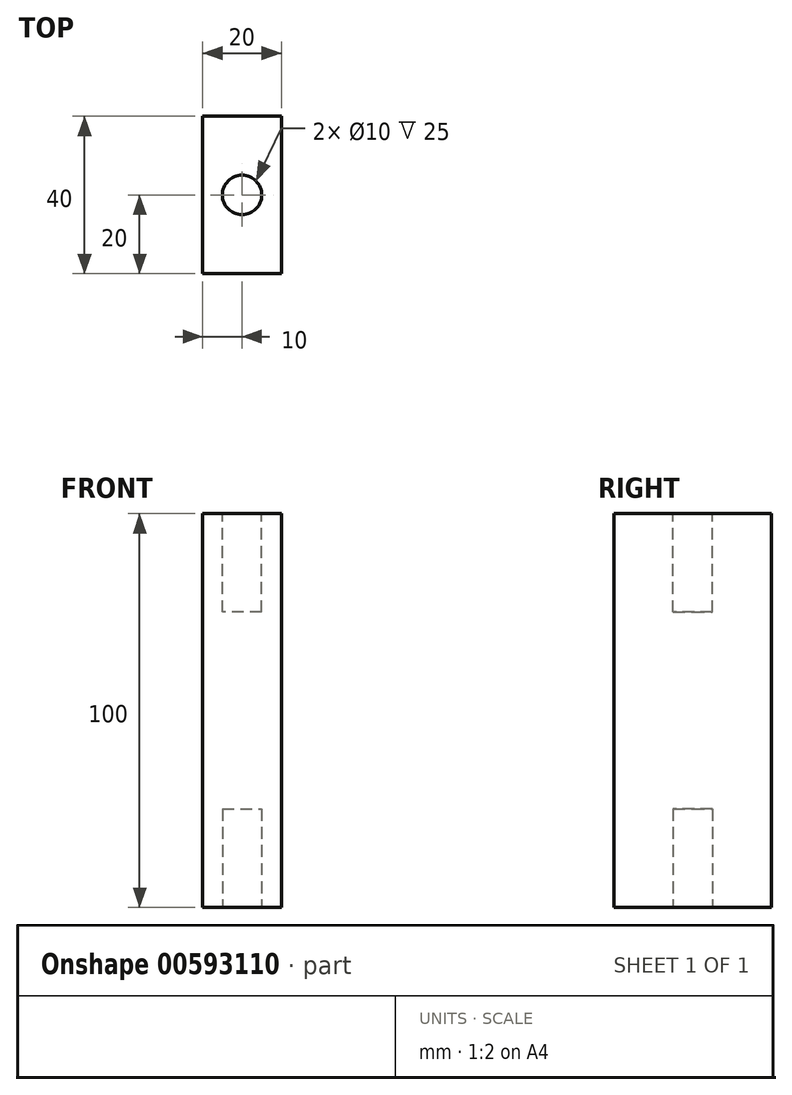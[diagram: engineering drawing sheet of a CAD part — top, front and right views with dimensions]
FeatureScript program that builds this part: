
annotation { "Feature Type Name" : "Feature", "Feature Type Description" : "" }
export const myFeature = defineFeature(function(context is Context, id is Id, definition is map)
    precondition{}
    {
        {
            var Q0;
            Q0=qCreatedBy(makeId("Top.planeOp"),FACE);
            var sketch = newSketch(context, id + "F0", { "sketchPlane" : qUnion([Q0])});
            skLineSegment(sketch, "E0.bottom", {"start": v(10, 20) * mm, "end": v(-10, 20) * mm});
            skLineSegment(sketch, "E0.top", {"start": v(10, -20) * mm, "end": v(-10, -20) * mm});
            skLineSegment(sketch, "E0.left", {"start": v(10, 20) * mm, "end": v(10, -20) * mm});
            skLineSegment(sketch, "E0.right", {"start": v(-10, 20) * mm, "end": v(-10, -20) * mm});
            skPoint(sketch, "E0.middle", {"position": v(0, 0) * mm});
            skSolve(sketch);
        }
        {
            var Q0;
            Q0=qSketchRegion(id+"F0",true);
            extrude(context, id + "F1", {"entities" : qUnion([Q0]), "depth" : 100 * mm, "offsetDistance" : 25 * mm});
        }
        {
            var Q0;
            Q0=makeQuery(id+"F1.opExtrude","CAP_FACE",FACE,{"disambiguationData":[OSD([sQuery(id+"F0.wireOp",EDGE,"E0.bottom"),sQuery(id+"F0.wireOp",EDGE,"E0.top"),sQuery(id+"F0.wireOp",EDGE,"E0.left"),sQuery(id+"F0.wireOp",EDGE,"E0.right")])],"isStart":false});
            var sketch = newSketch(context, id + "F2", { "sketchPlane" : qUnion([Q0])});
            skCircle(sketch, "E1", {"center": v(0, 0) * mm, "radius": 5 * mm});
            skSolve(sketch);
        }
        {
            var Q0;
            Q0=qSketchRegion(id+"F2",true);
            extrude(context, id + "F3", {"entities" : qUnion([Q0]), "operationType" : NewBodyOperationType.REMOVE, "oppositeDirection" : true, "depth" : 25 * mm, "offsetDistance" : 25 * mm});
        }
        {
            var Q0;
            Q0=makeQuery(id+"F1.opExtrude","CAP_FACE",FACE,{"disambiguationData":[OSD([sQuery(id+"F0.wireOp",EDGE,"E0.bottom"),sQuery(id+"F0.wireOp",EDGE,"E0.top"),sQuery(id+"F0.wireOp",EDGE,"E0.left"),sQuery(id+"F0.wireOp",EDGE,"E0.right")])],"isStart":true});
            var sketch = newSketch(context, id + "F4", { "sketchPlane" : qUnion([Q0])});
            skCircle(sketch, "E2", {"center": v(0, 0) * mm, "radius": 5 * mm});
            skSolve(sketch);
        }
        {
            var Q0;
            Q0=qSketchRegion(id+"F4",true);
            extrude(context, id + "F5", {"entities" : qUnion([Q0]), "operationType" : NewBodyOperationType.REMOVE, "oppositeDirection" : true, "depth" : 25 * mm, "offsetDistance" : 25 * mm});
        }
    });
